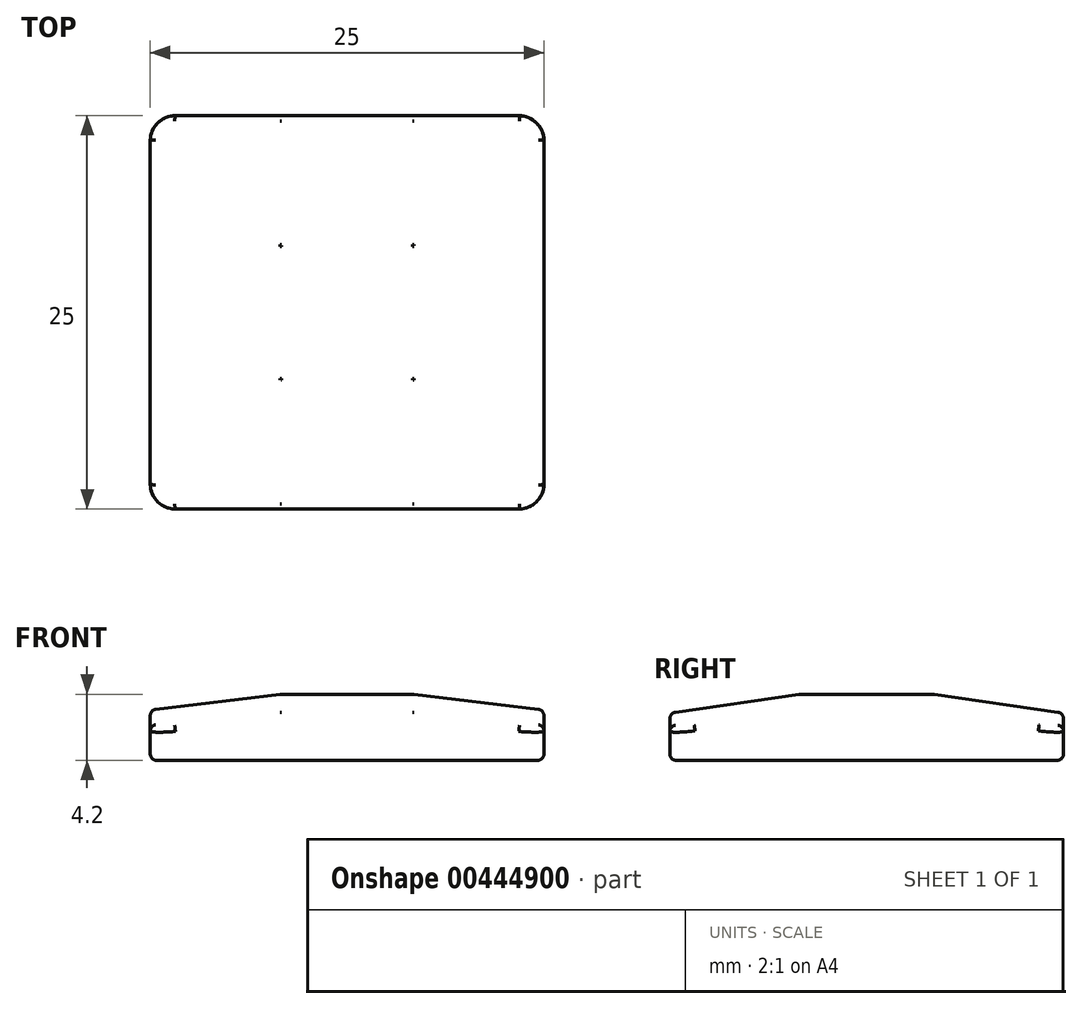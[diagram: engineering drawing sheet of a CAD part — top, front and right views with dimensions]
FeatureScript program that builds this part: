
annotation { "Feature Type Name" : "Feature", "Feature Type Description" : "" }
export const myFeature = defineFeature(function(context is Context, id is Id, definition is map)
    precondition{}
    {
        {
            var Q0;
            Q0=qCreatedBy(makeId("Top.planeOp"),FACE);
            var sketch = newSketch(context, id + "F0", { "sketchPlane" : qUnion([Q0])});
            skLineSegment(sketch, "E0.bottom", {"start": v(-12.5, 12.5) * mm, "end": v(12.5, 12.5) * mm});
            skLineSegment(sketch, "E0.top", {"start": v(-12.5, -12.5) * mm, "end": v(12.5, -12.5) * mm});
            skLineSegment(sketch, "E0.left", {"start": v(-12.5, 12.5) * mm, "end": v(-12.5, -12.5) * mm});
            skLineSegment(sketch, "E0.right", {"start": v(12.5, 12.5) * mm, "end": v(12.5, -12.5) * mm});
            skPoint(sketch, "E0.middle", {"position": v(0, 0) * mm});
            skSolve(sketch);
        }
        {
            var Q0;
            Q0 = qSketchRegion(id + "F0", true);
            extrude(context, id + "F1", {"entities" : qUnion([Q0]), "depth" : 3 * mm});
        }
        {
            var Q0;
            Q0=makeQuery(id+"F1.opExtrude","SWEPT_FACE",FACE,{"disambiguationData":[OSD([sQuery(id+"F0.wireOp",EDGE,"E0.right")])]});
            var sketch = newSketch(context, id + "F2", { "sketchPlane" : qUnion([Q0])});
            skLineSegment(sketch, "E1", {"start": v(-12.5, 3) * mm, "end": v(-4.25, 4.2) * mm});
            skLineSegment(sketch, "E2", {"start": v(-4.25, 4.2) * mm, "end": v(4.25, 4.2) * mm});
            skLineSegment(sketch, "E3", {"start": v(4.25, 4.2) * mm, "end": v(12.5, 3) * mm});
            skLineSegment(sketch, "E4", {"start": v(0, 0) * mm, "end": v(0, 4.2) * mm});
            skSolve(sketch);
        }
        {
            var Q0;
            {var subQ0=sQuery(id+"F2.wireOp",EDGE,"E3");Q0=makeQuery(id+"F2.imprint","IMPRINT",FACE,{"disambiguationData":[TD([[makeQuery(id+"F2.imprint","IMPRINT",EDGE,{"derivedFrom":subQ0}),-1.0]])]});}
            var Q1;
            {var subQ0=sQuery(id+"F2.wireOp",EDGE,"E1");Q1=makeQuery(id+"F2.imprint","IMPRINT",FACE,{"disambiguationData":[TD([[makeQuery(id+"F2.imprint","IMPRINT",EDGE,{"derivedFrom":subQ0}),-1.0]])]});}
            var Q2;
            Q2=makeQuery(id+"F1.opExtrude","SWEPT_FACE",FACE,{"disambiguationData":[OSD([sQuery(id+"F0.wireOp",EDGE,"E0.left")])]});
            extrude(context, id + "F3", {"entities" : qUnion([Q0, Q1]), "operationType" : NewBodyOperationType.ADD, "endBound" : BoundingType.UP_TO_SURFACE, "oppositeDirection" : true, "endBoundEntityFace" : qUnion([Q2]), "depth" : 25 * mm});
        }
        {
            var Q0;
            Q0=makeQuery(id+"F3.opExtrude","CAP_EDGE",EDGE,{"disambiguationData":[OSD([sQuery(id+"F2.wireOp",EDGE,"E2")])],"isStart":false});
            var Q1;
            Q1=makeQuery(id+"F3.opExtrude","CAP_EDGE",EDGE,{"disambiguationData":[OSD([sQuery(id+"F2.wireOp",EDGE,"E1")])],"isStart":false});
            var Q2;
            Q2=makeQuery(id+"F3.opExtrude","CAP_EDGE",EDGE,{"disambiguationData":[OSD([sQuery(id+"F2.wireOp",EDGE,"E3")])],"isStart":false});
            var Q3;
            Q3=makeQuery(id+"F3.opExtrude","CAP_EDGE",EDGE,{"disambiguationData":[OSD([sQuery(id+"F2.wireOp",EDGE,"E3")])],"isStart":true});
            var Q4;
            Q4=makeQuery(id+"F3.opExtrude","CAP_EDGE",EDGE,{"disambiguationData":[OSD([sQuery(id+"F2.wireOp",EDGE,"E2")])],"isStart":true});
            var Q5;
            Q5=makeQuery(id+"F3.opExtrude","CAP_EDGE",EDGE,{"disambiguationData":[OSD([sQuery(id+"F2.wireOp",EDGE,"E1")])],"isStart":true});
            chamfer(context, id + "F4", {"entities" : qUnion([Q0, Q1, Q2, Q3, Q4, Q5]), "chamferType" : ChamferType.TWO_OFFSETS, "width1" : 8.3 * mm, "oppositeDirection" : false, "width2" : 1 * mm, "tangentPropagation" : true});
        }
        {
            var Q0;
            Q0=makeQuery(id+"F1.opExtrude","SWEPT_EDGE",EDGE,{"disambiguationData":[OSD([sQuery(id+"F0.wireOp",EDGE,"E0.top"),sQuery(id+"F0.wireOp",EDGE,"E0.left")])]});
            var Q1;
            Q1=makeQuery(id+"F1.opExtrude","SWEPT_EDGE",EDGE,{"disambiguationData":[OSD([sQuery(id+"F0.wireOp",EDGE,"E0.top"),sQuery(id+"F0.wireOp",EDGE,"E0.right")])]});
            var Q2;
            Q2=makeQuery(id+"F1.opExtrude","SWEPT_EDGE",EDGE,{"disambiguationData":[OSD([sQuery(id+"F0.wireOp",EDGE,"E0.bottom"),sQuery(id+"F0.wireOp",EDGE,"E0.right")])]});
            var Q3;
            Q3=makeQuery(id+"F1.opExtrude","SWEPT_EDGE",EDGE,{"disambiguationData":[OSD([sQuery(id+"F0.wireOp",EDGE,"E0.bottom"),sQuery(id+"F0.wireOp",EDGE,"E0.left")])]});
            fillet(context, id + "F5", {"entities" : qUnion([Q0, Q1, Q2, Q3]), "radius" : 1.6 * mm, "tangentPropagation" : true, "allowEdgeOverflow" : false});
        }
        {
            var Q0;
            {var subQ0=sQuery(id+"F2.wireOp",EDGE,"E3");Q0=makeQuery(id+"F4.opChamfer","BLEND_EDGE",EDGE,{"blendedFrom":[makeQuery(id+"F3.opExtrude","CAP_EDGE",EDGE,{"disambiguationData":[OSD([subQ0])],"isStart":false}),makeQuery(id+"F3.opExtrude","SWEPT_FACE",FACE,{"disambiguationData":[OSD([subQ0])]})],"blendedInto":[makeQuery(id+"F3.opExtrude","SWEPT_FACE",FACE,{"disambiguationData":[OSD([subQ0])]})]});}
            var Q1;
            {var subQ0=sQuery(id+"F2.wireOp",EDGE,"E3");Q1=makeQuery(id+"F4.opChamfer","BLEND_EDGE",EDGE,{"blendedFrom":[makeQuery(id+"F3.opExtrude","CAP_EDGE",EDGE,{"disambiguationData":[OSD([subQ0])],"isStart":true}),makeQuery(id+"F3.opExtrude","SWEPT_FACE",FACE,{"disambiguationData":[OSD([subQ0])]})],"blendedInto":[makeQuery(id+"F3.opExtrude","SWEPT_FACE",FACE,{"disambiguationData":[OSD([subQ0])]})]});}
            var Q2;
            Q2=makeQuery(id+"F4.opChamfer","BLEND_EDGE",EDGE,{"blendedFrom":[makeQuery(id+"F3.opExtrude","CAP_EDGE",EDGE,{"disambiguationData":[OSD([sQuery(id+"F2.wireOp",EDGE,"E2")])],"isStart":true}),makeQuery(id+"F3.opExtrude","CAP_EDGE",EDGE,{"disambiguationData":[OSD([sQuery(id+"F2.wireOp",EDGE,"E3")])],"isStart":true})],"blendedInto":[]});
            var Q3;
            Q3=makeQuery(id+"F3.opExtrude","SWEPT_EDGE",EDGE,{"disambiguationData":[OSD([sQuery(id+"F2.wireOp",EDGE,"E2"),sQuery(id+"F2.wireOp",EDGE,"E3")])]});
            var Q4;
            Q4=makeQuery(id+"F4.opChamfer","BLEND_EDGE",EDGE,{"blendedFrom":[makeQuery(id+"F3.opExtrude","CAP_EDGE",EDGE,{"disambiguationData":[OSD([sQuery(id+"F2.wireOp",EDGE,"E2")])],"isStart":false}),makeQuery(id+"F3.opExtrude","CAP_EDGE",EDGE,{"disambiguationData":[OSD([sQuery(id+"F2.wireOp",EDGE,"E3")])],"isStart":false})],"blendedInto":[]});
            var Q5;
            {var subQ0=sQuery(id+"F2.wireOp",EDGE,"E2");Q5=makeQuery(id+"F4.opChamfer","BLEND_EDGE",EDGE,{"blendedFrom":[makeQuery(id+"F3.opExtrude","CAP_EDGE",EDGE,{"disambiguationData":[OSD([subQ0])],"isStart":false}),makeQuery(id+"F3.opExtrude","SWEPT_FACE",FACE,{"disambiguationData":[OSD([subQ0])]})],"blendedInto":[makeQuery(id+"F3.opExtrude","SWEPT_FACE",FACE,{"disambiguationData":[OSD([subQ0])]})]});}
            var Q6;
            {var subQ0=sQuery(id+"F2.wireOp",EDGE,"E2");Q6=makeQuery(id+"F4.opChamfer","BLEND_EDGE",EDGE,{"blendedFrom":[makeQuery(id+"F3.opExtrude","CAP_EDGE",EDGE,{"disambiguationData":[OSD([subQ0])],"isStart":true}),makeQuery(id+"F3.opExtrude","SWEPT_FACE",FACE,{"disambiguationData":[OSD([subQ0])]})],"blendedInto":[makeQuery(id+"F3.opExtrude","SWEPT_FACE",FACE,{"disambiguationData":[OSD([subQ0])]})]});}
            var Q7;
            Q7=makeQuery(id+"F4.opChamfer","BLEND_EDGE",EDGE,{"blendedFrom":[makeQuery(id+"F3.opExtrude","CAP_EDGE",EDGE,{"disambiguationData":[OSD([sQuery(id+"F2.wireOp",EDGE,"E1")])],"isStart":true}),makeQuery(id+"F3.opExtrude","CAP_EDGE",EDGE,{"disambiguationData":[OSD([sQuery(id+"F2.wireOp",EDGE,"E2")])],"isStart":true})],"blendedInto":[]});
            var Q8;
            {var subQ0=sQuery(id+"F2.wireOp",EDGE,"E1");Q8=makeQuery(id+"F4.opChamfer","BLEND_EDGE",EDGE,{"blendedFrom":[makeQuery(id+"F3.opExtrude","CAP_EDGE",EDGE,{"disambiguationData":[OSD([subQ0])],"isStart":true}),makeQuery(id+"F3.opExtrude","SWEPT_FACE",FACE,{"disambiguationData":[OSD([subQ0])]})],"blendedInto":[makeQuery(id+"F3.opExtrude","SWEPT_FACE",FACE,{"disambiguationData":[OSD([subQ0])]})]});}
            var Q9;
            Q9=makeQuery(id+"F3.opExtrude","SWEPT_EDGE",EDGE,{"disambiguationData":[OSD([sQuery(id+"F2.wireOp",EDGE,"E1"),sQuery(id+"F2.wireOp",EDGE,"E2")])]});
            var Q10;
            {var subQ0=sQuery(id+"F2.wireOp",EDGE,"E1");Q10=makeQuery(id+"F4.opChamfer","BLEND_EDGE",EDGE,{"blendedFrom":[makeQuery(id+"F3.opExtrude","CAP_EDGE",EDGE,{"disambiguationData":[OSD([subQ0])],"isStart":false}),makeQuery(id+"F3.opExtrude","SWEPT_FACE",FACE,{"disambiguationData":[OSD([subQ0])]})],"blendedInto":[makeQuery(id+"F3.opExtrude","SWEPT_FACE",FACE,{"disambiguationData":[OSD([subQ0])]})]});}
            var Q11;
            Q11=makeQuery(id+"F4.opChamfer","BLEND_EDGE",EDGE,{"blendedFrom":[makeQuery(id+"F3.opExtrude","CAP_EDGE",EDGE,{"disambiguationData":[OSD([sQuery(id+"F2.wireOp",EDGE,"E1")])],"isStart":false}),makeQuery(id+"F3.opExtrude","CAP_EDGE",EDGE,{"disambiguationData":[OSD([sQuery(id+"F2.wireOp",EDGE,"E2")])],"isStart":false})],"blendedInto":[]});
            fillet(context, id + "F6", {"entities" : qUnion([Q0, Q1, Q2, Q3, Q4, Q5, Q6, Q7, Q8, Q9, Q10, Q11]), "radius" : 0.8 * mm, "tangentPropagation" : true, "allowEdgeOverflow" : false});
        }
        {
            var Q0;
            {var subQ0=sQuery(id+"F2.wireOp",EDGE,"E3");Q0=makeQuery(id+"F4.opChamfer","BLEND_EDGE",EDGE,{"blendedFrom":[makeQuery(id+"F3.opExtrude","CAP_EDGE",EDGE,{"disambiguationData":[OSD([subQ0])],"isStart":false}),makeQuery(id+"F3.boolean.opBoolean","MERGE",FACE,{"derivedFrom":[makeQuery(id+"F1.opExtrude","SWEPT_FACE",FACE,{"disambiguationData":[OSD([sQuery(id+"F0.wireOp",EDGE,"E0.left")])]}),makeQuery(id+"F3.opExtrude","CAP_FACE",FACE,{"disambiguationData":[OSD([sQuery(id+"F0.wireOp",EDGE,"E0.right"),sQuery(id+"F2.wireOp",EDGE,"E1"),sQuery(id+"F2.wireOp",EDGE,"E2"),subQ0])],"isStart":false})]})],"blendedInto":[makeQuery(id+"F3.boolean.opBoolean","MERGE",FACE,{"derivedFrom":[makeQuery(id+"F1.opExtrude","SWEPT_FACE",FACE,{"disambiguationData":[OSD([sQuery(id+"F0.wireOp",EDGE,"E0.left")])]}),makeQuery(id+"F3.opExtrude","CAP_FACE",FACE,{"disambiguationData":[OSD([sQuery(id+"F0.wireOp",EDGE,"E0.right"),sQuery(id+"F2.wireOp",EDGE,"E1"),sQuery(id+"F2.wireOp",EDGE,"E2"),subQ0])],"isStart":false})]})]});}
            var Q1;
            Q1=makeQuery(id+"F1.opExtrude","CAP_EDGE",EDGE,{"disambiguationData":[OSD([sQuery(id+"F0.wireOp",EDGE,"E0.left")])],"isStart":true});
            fillet(context, id + "F7", {"entities" : qUnion([Q0, Q1]), "radius" : 0.4 * mm, "tangentPropagation" : true, "allowEdgeOverflow" : false});
        }
    });
